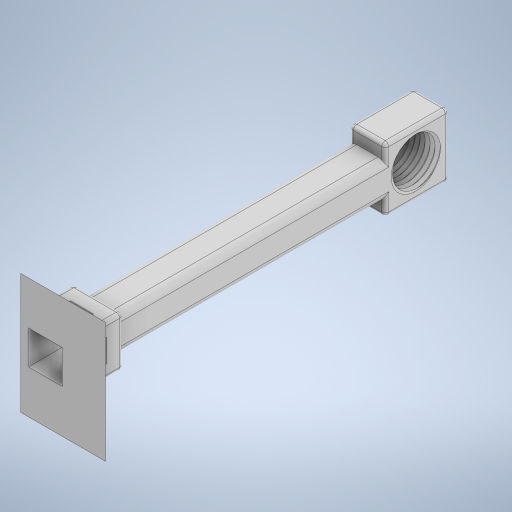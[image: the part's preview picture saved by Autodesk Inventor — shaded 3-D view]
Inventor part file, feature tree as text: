
AUTODESK INVENTOR PART (.ipt)
format: ipt  version: 2024 (Build 280153000, 153)  size: 620,544 bytes
history: native  units: mm
features: sketch x16, extrude x15, fillet x3, mirror x2, other x1
ambient origin geometry x8: Origin, YZ Plane, XZ Plane, XY Plane, X Axis, Y Axis, Z Axis, Center Point
bodies: Volumenkörper1 (feature_tree)
feature tree (37):
  extrude  "Extrusion1"  Depth=10.0mm
  extrude  "Extrusion2"  Depth=10.0mm
  extrude  "Extrusion3"  Depth=18.0mm TaperAngle=0.0deg
  extrude  "Extrusion4"  Depth=9.0mm TaperAngle=0.0deg
  other  "Spirale1"
  extrude  "Extrusion6"  Depth=9.0mm TaperAngle=0.0deg
  extrude  "Extrusion12"  Depth=10.0mm
  mirror  "Spiegeln1"
  extrude  "Extrusion13"  Depth=0.2mm
  mirror  "Spiegeln2"
  extrude  "Extrusion7"  Depth=1.0mm
  extrude  "Extrusion8"  Depth=9.75mm TaperAngle=0.0deg
  extrude  "Extrusion9"  Depth=1.5mm
  extrude  "Extrusion14"  Depth=5.0mm
  extrude  "Extrusion15"  Depth=1.5mm
  extrude  "Extrusion16"  Depth=1.5mm
  extrude  "Extrusion17"  Depth=5.0mm
  extrude  "Extrusion18"  Depth=10.0mm TaperAngle=0.0deg
  fillet  "Rundung3"  Radius=10.0mm
  fillet  "Rundung4"  Radius=15.0mm
  fillet  "Rundung5"  Radius=2.0mm
  sketch  "Skizze1"  dims[d0=10.0mm d1=10.0mm]
  sketch  "Skizze2"  dims[d2=91.0mm d3=0.0mm d4=10.0mm]
  sketch  "Skizze3"  dims[d5=18.0mm d6=18.0mm d7=0.0mm]
  sketch  "Skizze4"  dims[d8=15.0mm d9=9.0mm d10=0.0mm]
  sketch  "Skizze5"  dims[d17=12.2mm d18=9.0mm d19=0.0mm]
  sketch  "Skizze7"  dims[d22=1.4mm d23=11.0mm d24=10.0mm d25=0.0mm d26=90.0deg d27=90.0deg d28=0.0mm d29=0.0mm d33=1.7mm]
  sketch  "Skizze8"  dims[d34=60.0deg d35=0.2mm]
  sketch  "Skizze9"  dims[d36=1.0mm d37=0.0mm d39=9.5mm]
  sketch  "Skizze10"  dims[d40=9.5mm d41=9.75mm d42=0.0mm]
  sketch  "Skizze16"  dims[d43=1.5mm d44=1.5mm]
  sketch  "Skizze17"  dims[d45=5.0mm d46=5.0mm]
  sketch  "Skizze18"  dims[d47=1.5mm d48=1.5mm]
  sketch  "Skizze20"  dims[d49=1.5mm d50=1.5mm]
  sketch  "Skizze22"  dims[d51=5.0mm d52=5.0mm]
  sketch  "Skizze23"  dims[d53=1.2mm d54=0.0mm d55=2.0mm d56=0.0mm d65=10.0mm d66=15.0mm d67=2.0mm d68=0.0mm]
  sketch  "Skizze24"  dims[d69=2.0mm d70=0.0mm d71=10.0mm d72=0.0mm d73=10.0mm d74=7.0mm d75=10.0mm d76=24.0mm d77=0.0mm d78=10.0mm d79=24.0mm d80=0.0mm d81=24.0mm d82=0.0mm d83=60.0mm d84=0.0mm d85=10.0mm d86=0.0mm d87=2.0mm d88=1.0mm d89=1.0mm d38=0.0mm]
